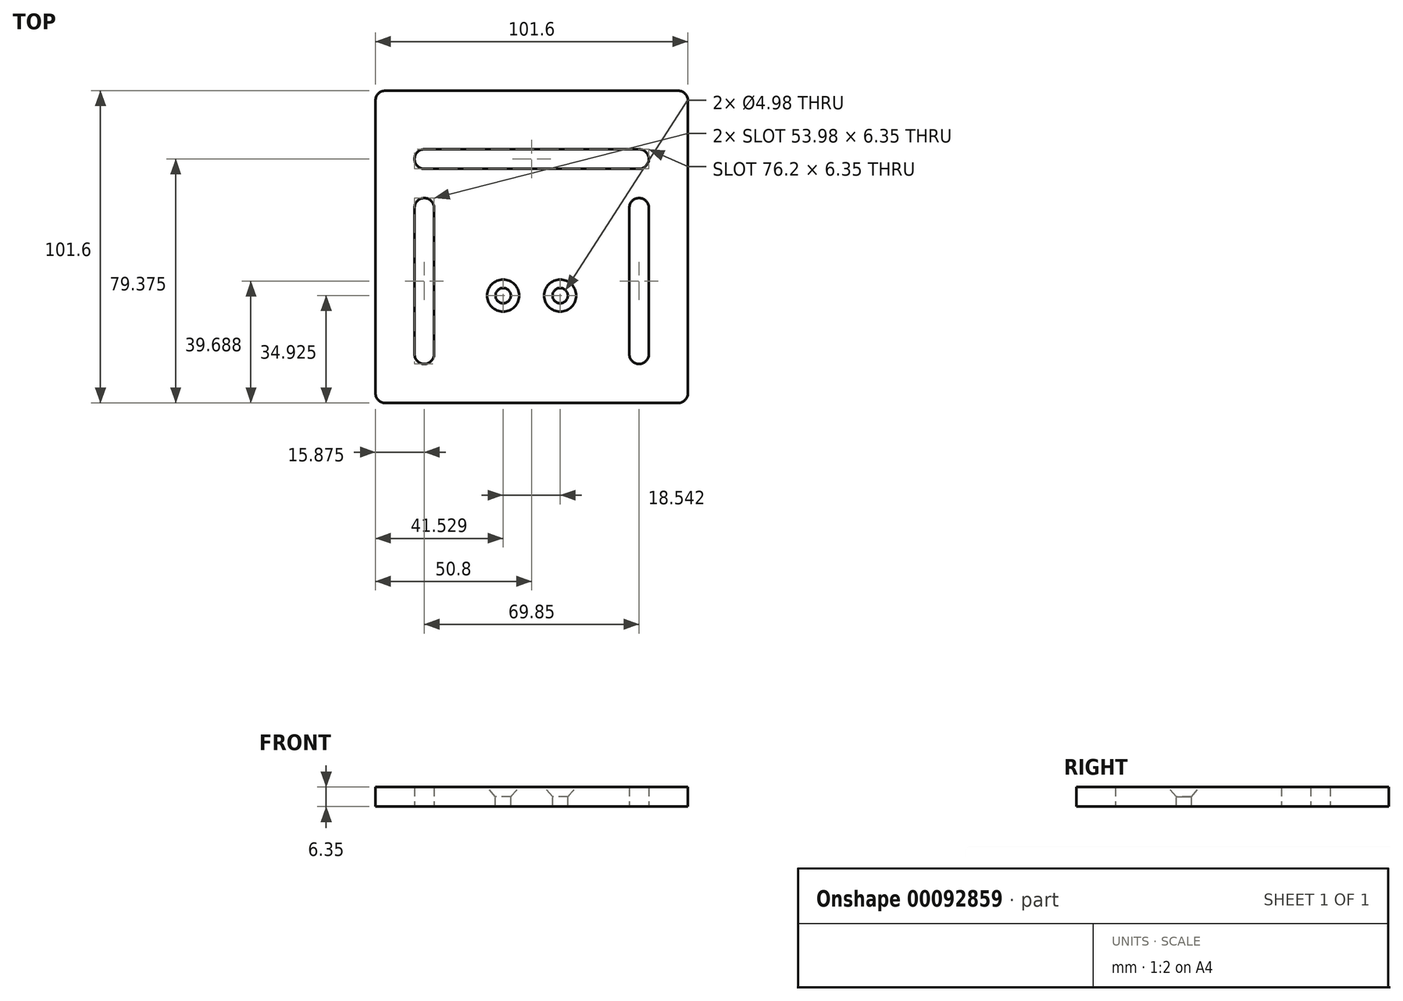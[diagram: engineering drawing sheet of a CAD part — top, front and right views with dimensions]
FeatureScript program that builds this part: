
annotation { "Feature Type Name" : "Feature", "Feature Type Description" : "" }
export const myFeature = defineFeature(function(context is Context, id is Id, definition is map)
    precondition{}
    {
        {
            var Q0;
            Q0=qCreatedBy(makeId("Top.planeOp"),FACE);
            var sketch = newSketch(context, id + "F0", { "sketchPlane" : qUnion([Q0])});
            skLineSegment(sketch, "E0.bottom", {"start": v(50.8, -50.8) * mm, "end": v(-50.8, -50.8) * mm});
            skLineSegment(sketch, "E0.top", {"start": v(50.8, 50.8) * mm, "end": v(-50.8, 50.8) * mm});
            skLineSegment(sketch, "E0.left", {"start": v(50.8, -50.8) * mm, "end": v(50.8, 50.8) * mm});
            skLineSegment(sketch, "E0.right", {"start": v(-50.8, -50.8) * mm, "end": v(-50.8, 50.8) * mm});
            skPoint(sketch, "E0.middle", {"position": v(0, 0) * mm});
            skLineSegment(sketch, "E1", {"start": v(-50.8, 28.58) * mm, "end": v(50.8, 28.58) * mm, "construction": true});
            skLineSegment(sketch, "E2", {"start": v(-34.93, 50.8) * mm, "end": v(-34.93, -50.8) * mm, "construction": true});
            skLineSegment(sketch, "E3", {"start": v(34.93, 50.8) * mm, "end": v(34.93, -50.8) * mm, "construction": true});
            skLineSegment(sketch, "E4", {"start": v(-50.8, -34.93) * mm, "end": v(50.8, -34.92) * mm, "construction": true});
            skLineSegment(sketch, "E5", {"start": v(-50.8, 12.7) * mm, "end": v(50.8, 12.7) * mm, "construction": true});
            skLineSegment(sketch, "E6", {"start": v(-34.93, 28.58) * mm, "end": v(34.93, 28.58) * mm});
            skLineSegment(sketch, "E7", {"start": v(-34.93, 12.7) * mm, "end": v(-34.92, -34.93) * mm});
            skLineSegment(sketch, "E8", {"start": v(34.93, 12.7) * mm, "end": v(34.93, -34.93) * mm});
            skArc(sketch, "E9.0.startCap", {"start": v(-34.93, 25.4) * mm, "mid": v(-38.1, 28.58) * mm, "end": v(-34.93, 31.75) * mm});
            skArc(sketch, "E9.0.endCap", {"start": v(34.93, 31.75) * mm, "mid": v(38.1, 28.57) * mm, "end": v(34.93, 25.4) * mm});
            skLineSegment(sketch, "E9.0.left", {"start": v(-34.93, 31.75) * mm, "end": v(34.93, 31.75) * mm});
            skLineSegment(sketch, "E9.0.right", {"start": v(-34.93, 25.4) * mm, "end": v(34.93, 25.4) * mm});
            skArc(sketch, "E9.1.startCap", {"start": v(-38.1, 12.7) * mm, "mid": v(-34.93, 15.87) * mm, "end": v(-31.75, 12.7) * mm});
            skArc(sketch, "E9.1.endCap", {"start": v(-31.75, -34.93) * mm, "mid": v(-34.92, -38.1) * mm, "end": v(-38.1, -34.93) * mm});
            skLineSegment(sketch, "E9.1.left", {"start": v(-31.75, 12.7) * mm, "end": v(-31.75, -34.93) * mm});
            skLineSegment(sketch, "E9.1.right", {"start": v(-38.1, 12.7) * mm, "end": v(-38.1, -34.93) * mm});
            skArc(sketch, "E9.2.startCap", {"start": v(31.75, 12.7) * mm, "mid": v(34.93, 15.88) * mm, "end": v(38.1, 12.7) * mm});
            skArc(sketch, "E9.2.endCap", {"start": v(38.1, -34.93) * mm, "mid": v(34.93, -38.1) * mm, "end": v(31.75, -34.93) * mm});
            skLineSegment(sketch, "E9.2.left", {"start": v(38.1, 12.7) * mm, "end": v(38.1, -34.93) * mm});
            skLineSegment(sketch, "E9.2.right", {"start": v(31.75, 12.7) * mm, "end": v(31.75, -34.93) * mm});
            skSolve(sketch);
        }
        {
            var Q0;
            Q0=makeQuery(id+"F0.imprint","IMPRINT",FACE,{"disambiguationData":[TD([[makeQuery(id+"F0.imprint","IMPRINT",EDGE,{"derivedFrom":sQuery(id+"F0.wireOp",EDGE,"E0.bottom")}),-1.0]])]});
            extrude(context, id + "F1", {"entities" : qUnion([Q0]), "depth" : 6.35 * mm});
        }
        {
            var Q0;
            Q0=makeQuery(id+"F1.opExtrude","CAP_FACE",FACE,{"disambiguationData":[OSD([sQuery(id+"F0.wireOp",EDGE,"E0.bottom"),sQuery(id+"F0.wireOp",EDGE,"E0.top"),sQuery(id+"F0.wireOp",EDGE,"E0.left"),sQuery(id+"F0.wireOp",EDGE,"E0.right"),sQuery(id+"F0.wireOp",EDGE,"E9.0.startCap"),sQuery(id+"F0.wireOp",EDGE,"E9.0.endCap"),sQuery(id+"F0.wireOp",EDGE,"E9.0.left"),sQuery(id+"F0.wireOp",EDGE,"E9.0.right"),sQuery(id+"F0.wireOp",EDGE,"E9.1.startCap"),sQuery(id+"F0.wireOp",EDGE,"E9.1.endCap"),sQuery(id+"F0.wireOp",EDGE,"E9.1.left"),sQuery(id+"F0.wireOp",EDGE,"E9.1.right"),sQuery(id+"F0.wireOp",EDGE,"E9.2.startCap"),sQuery(id+"F0.wireOp",EDGE,"E9.2.endCap"),sQuery(id+"F0.wireOp",EDGE,"E9.2.left"),sQuery(id+"F0.wireOp",EDGE,"E9.2.right")])],"isStart":false});
            var sketch = newSketch(context, id + "F2", { "sketchPlane" : qUnion([Q0])});
            skLineSegment(sketch, "E10", {"start": v(-50.8, -15.88) * mm, "end": v(50.8, -15.87) * mm, "construction": true});
            skLineSegment(sketch, "E11", {"start": v(9.27, 50.8) * mm, "end": v(9.27, -50.8) * mm, "construction": true});
            skLineSegment(sketch, "E12", {"start": v(-9.27, 50.8) * mm, "end": v(-9.27, -50.8) * mm, "construction": true});
            skPoint(sketch, "E13", {"position": v(-9.27, -15.87) * mm});
            skPoint(sketch, "E14", {"position": v(9.27, -15.87) * mm});
            skSolve(sketch);
        }
        {
            var Q0;
            Q0=sQuery(id+"F2.wireOp",VERTEX,"E13");
            var Q1;
            Q1=sQuery(id+"F2.wireOp",VERTEX,"E14");
            var Q2;
            Q2=makeQuery(id+"F1.opExtrude","SWEPT_BODY",BODY,{"disambiguationData":[OSD([sQuery(id+"F0.wireOp",EDGE,"E0.bottom"),sQuery(id+"F0.wireOp",EDGE,"E0.top"),sQuery(id+"F0.wireOp",EDGE,"E0.left"),sQuery(id+"F0.wireOp",EDGE,"E0.right"),sQuery(id+"F0.wireOp",EDGE,"E9.0.startCap"),sQuery(id+"F0.wireOp",EDGE,"E9.0.endCap"),sQuery(id+"F0.wireOp",EDGE,"E9.0.left"),sQuery(id+"F0.wireOp",EDGE,"E9.0.right"),sQuery(id+"F0.wireOp",EDGE,"E9.1.startCap"),sQuery(id+"F0.wireOp",EDGE,"E9.1.endCap"),sQuery(id+"F0.wireOp",EDGE,"E9.1.left"),sQuery(id+"F0.wireOp",EDGE,"E9.1.right"),sQuery(id+"F0.wireOp",EDGE,"E9.2.startCap"),sQuery(id+"F0.wireOp",EDGE,"E9.2.endCap"),sQuery(id+"F0.wireOp",EDGE,"E9.2.left"),sQuery(id+"F0.wireOp",EDGE,"E9.2.right")])]});
            hole(context, id + "F3", {"style" : HoleStyle.C_SINK, "endStyle" : HoleEndStyle.THROUGH, "standardTappedOrClearance" : lookupTablePath({ "standard" : "ANSI", "fit" : "Close", "size" : "#10", "type" : "Clearance" }), "standardBlindInLast" : lookupTablePath({ "fit" : "Close", "standard" : "ANSI", "size" : "#10", "type" : "Clearance" }), "holeDiameter" : 4.98 * mm, "cSinkDiameter" : 10.44 * mm, "cSinkAngle" : 82 * degree, "locations" : qUnion([Q0, Q1]), "scope" : qUnion([Q2]), "isTappedThrough" : true});
        }
        {
            var Q0;
            Q0=makeQuery(id+"F1.opExtrude","SWEPT_EDGE",EDGE,{"disambiguationData":[OSD([sQuery(id+"F0.wireOp",EDGE,"E0.bottom"),sQuery(id+"F0.wireOp",EDGE,"E0.right")])]});
            var Q1;
            Q1=makeQuery(id+"F1.opExtrude","SWEPT_EDGE",EDGE,{"disambiguationData":[OSD([sQuery(id+"F0.wireOp",EDGE,"E0.bottom"),sQuery(id+"F0.wireOp",EDGE,"E0.left")])]});
            var Q2;
            Q2=makeQuery(id+"F1.opExtrude","SWEPT_EDGE",EDGE,{"disambiguationData":[OSD([sQuery(id+"F0.wireOp",EDGE,"E0.top"),sQuery(id+"F0.wireOp",EDGE,"E0.right")])]});
            var Q3;
            Q3=makeQuery(id+"F1.opExtrude","SWEPT_EDGE",EDGE,{"disambiguationData":[OSD([sQuery(id+"F0.wireOp",EDGE,"E0.top"),sQuery(id+"F0.wireOp",EDGE,"E0.left")])]});
            fillet(context, id + "F4", {"entities" : qUnion([Q0, Q1, Q2, Q3]), "radius" : 3.17 * mm, "tangentPropagation" : true, "allowEdgeOverflow" : false});
        }
    });
